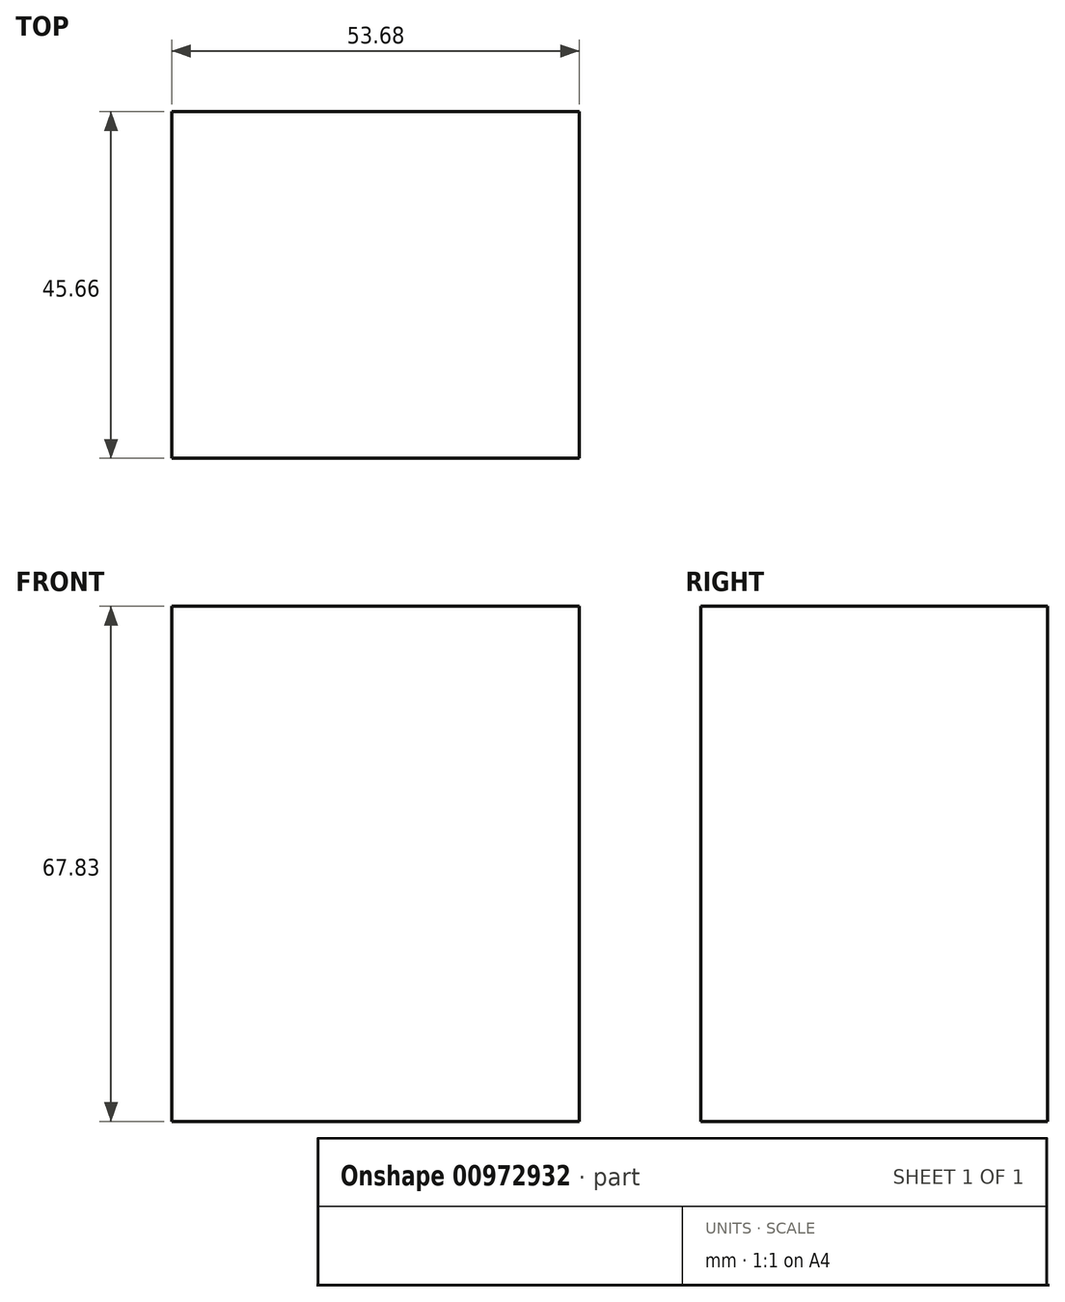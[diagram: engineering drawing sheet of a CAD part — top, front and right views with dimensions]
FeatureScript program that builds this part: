
annotation { "Feature Type Name" : "Feature", "Feature Type Description" : "" }
export const myFeature = defineFeature(function(context is Context, id is Id, definition is map)
    precondition{}
    {
        {
            var Q0;
            Q0=qCreatedBy(makeId("Front.planeOp"),FACE);
            var sketch = newSketch(context, id + "F0", { "sketchPlane" : qUnion([Q0])});
            skLineSegment(sketch, "E0.bottom", {"start": v(-19.23, 36.34) * mm, "end": v(34.45, 36.34) * mm});
            skLineSegment(sketch, "E0.top", {"start": v(-19.23, -31.5) * mm, "end": v(34.45, -31.5) * mm});
            skLineSegment(sketch, "E0.left", {"start": v(-19.23, 36.34) * mm, "end": v(-19.23, -31.5) * mm});
            skLineSegment(sketch, "E0.right", {"start": v(34.45, 36.34) * mm, "end": v(34.45, -31.5) * mm});
            skSolve(sketch);
        }
        {
            var Q0;
            Q0=makeQuery(id+"F0.imprint","IMPRINT",FACE,{"disambiguationData":[TD([[makeQuery(id+"F0.imprint","IMPRINT",EDGE,{"derivedFrom":sQuery(id+"F0.wireOp",EDGE,"E0.bottom")}),-1.0]])]});
            extrude(context, id + "F1", {"entities" : qUnion([Q0]), "depth" : 45.66 * mm, "offsetDistance" : 25.4 * mm});
        }
        {
            var Q0;
            Q0=makeQuery(id+"F1.opExtrude","SWEPT_FACE",FACE,{"disambiguationData":[OSD([sQuery(id+"F0.wireOp",EDGE,"E0.left")])]});
            var sketch = newSketch(context, id + "F2", { "sketchPlane" : qUnion([Q0])});
            skCircle(sketch, "E1", {"center": v(17.11, 0) * mm, "radius": 12.5 * mm});
            skSolve(sketch);
        }
        {
            var Q0;
            Q0 = qSketchRegion(id + "F2", true);
            extrude(context, id + "F3", {"entities" : qUnion([Q0]), "operationType" : NewBodyOperationType.ADD, "oppositeDirection" : true, "depth" : 30.57 * mm, "offsetDistance" : 25.4 * mm});
        }
    });
